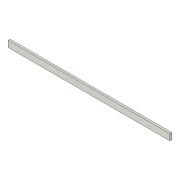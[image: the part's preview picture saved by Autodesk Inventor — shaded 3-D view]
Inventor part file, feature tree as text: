
AUTODESK INVENTOR PART (.ipt)
format: ipt  version: 2018 (Build 220112000, 112)  size: 71,680 bytes
history: native  units: in
note: dims shown in document units (in); Inventor stores cm internally (conversion verified against a paired STEP export)
features: extrude x1, sketch x1
ambient origin geometry x8: Origin, YZ Plane, XZ Plane, XY Plane, X Axis, Y Axis, Z Axis, Center Point
bodies: Solid1 (feature_tree)
feature tree (2):
  extrude  "Extrusion1"  Depth=3.0in
  sketch  "Sketch1"  dims[d0=1.0in d1=3.0in d2=78.0in d3=0.0in]
